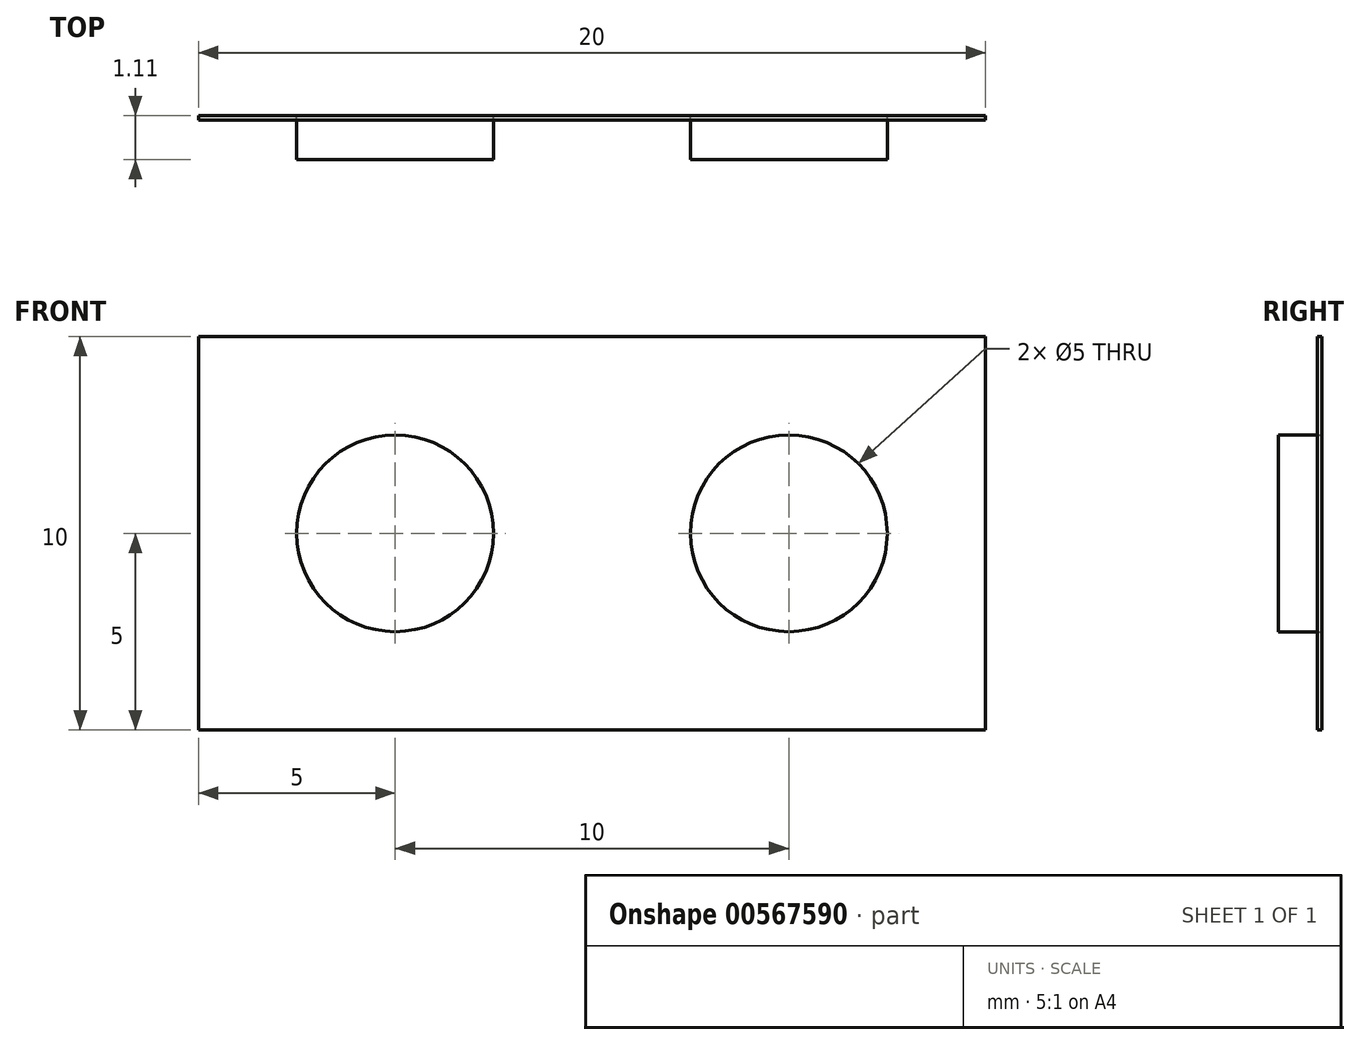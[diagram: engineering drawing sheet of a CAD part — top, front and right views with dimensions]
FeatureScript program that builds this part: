
annotation { "Feature Type Name" : "Feature", "Feature Type Description" : "" }
export const myFeature = defineFeature(function(context is Context, id is Id, definition is map)
    precondition{}
    {
        {
            var Q0;
            Q0=qCreatedBy(makeId("Front.planeOp"),FACE);
            var sketch = newSketch(context, id + "F0", { "sketchPlane" : qUnion([Q0])});
            skLineSegment(sketch, "E0.bottom", {"start": v(0, 0) * mm, "end": v(20, 0) * mm});
            skLineSegment(sketch, "E0.top", {"start": v(0, -10) * mm, "end": v(20, -10) * mm});
            skLineSegment(sketch, "E0.left", {"start": v(0, 0) * mm, "end": v(0, -10) * mm});
            skLineSegment(sketch, "E0.right", {"start": v(20, 0) * mm, "end": v(20, -10) * mm});
            skCircle(sketch, "E1", {"center": v(5, -5) * mm, "radius": 2.5 * mm});
            skCircle(sketch, "E2", {"center": v(15, -5) * mm, "radius": 2.5 * mm});
            skSolve(sketch);
        }
        {
            var Q0;
            Q0=makeQuery(id+"F0.imprint","IMPRINT",FACE,{"disambiguationData":[TD([[makeQuery(id+"F0.imprint","IMPRINT",EDGE,{"derivedFrom":sQuery(id+"F0.wireOp",EDGE,"E0.bottom")}),-1.0]])]});
            extrude(context, id + "F1", {"entities" : qUnion([Q0]), "depth" : 0.1 * mm, "offsetDistance" : 25 * mm});
        }
        {
            var Q0;
            Q0=makeQuery(id+"F1.opExtrude","CAP_FACE",FACE,{"disambiguationData":[OSD([sQuery(id+"F0.wireOp",EDGE,"E0.bottom"),sQuery(id+"F0.wireOp",EDGE,"E0.top"),sQuery(id+"F0.wireOp",EDGE,"E0.left"),sQuery(id+"F0.wireOp",EDGE,"E0.right"),sQuery(id+"F0.wireOp",EDGE,"E1"),sQuery(id+"F0.wireOp",EDGE,"E2")])],"isStart":false});
            var sketch = newSketch(context, id + "F2", { "sketchPlane" : qUnion([Q0])});
            skCircle(sketch, "E3", {"center": v(5, -5) * mm, "radius": 2.5 * mm});
            skCircle(sketch, "E4", {"center": v(15, -5) * mm, "radius": 2.5 * mm});
            skSolve(sketch);
        }
        {
            var Q0;
            Q0 = qSketchRegion(id + "F2", true);
            extrude(context, id + "F3", {"entities" : qUnion([Q0]), "depth" : 1 * mm, "offsetDistance" : 25 * mm});
        }
    });
